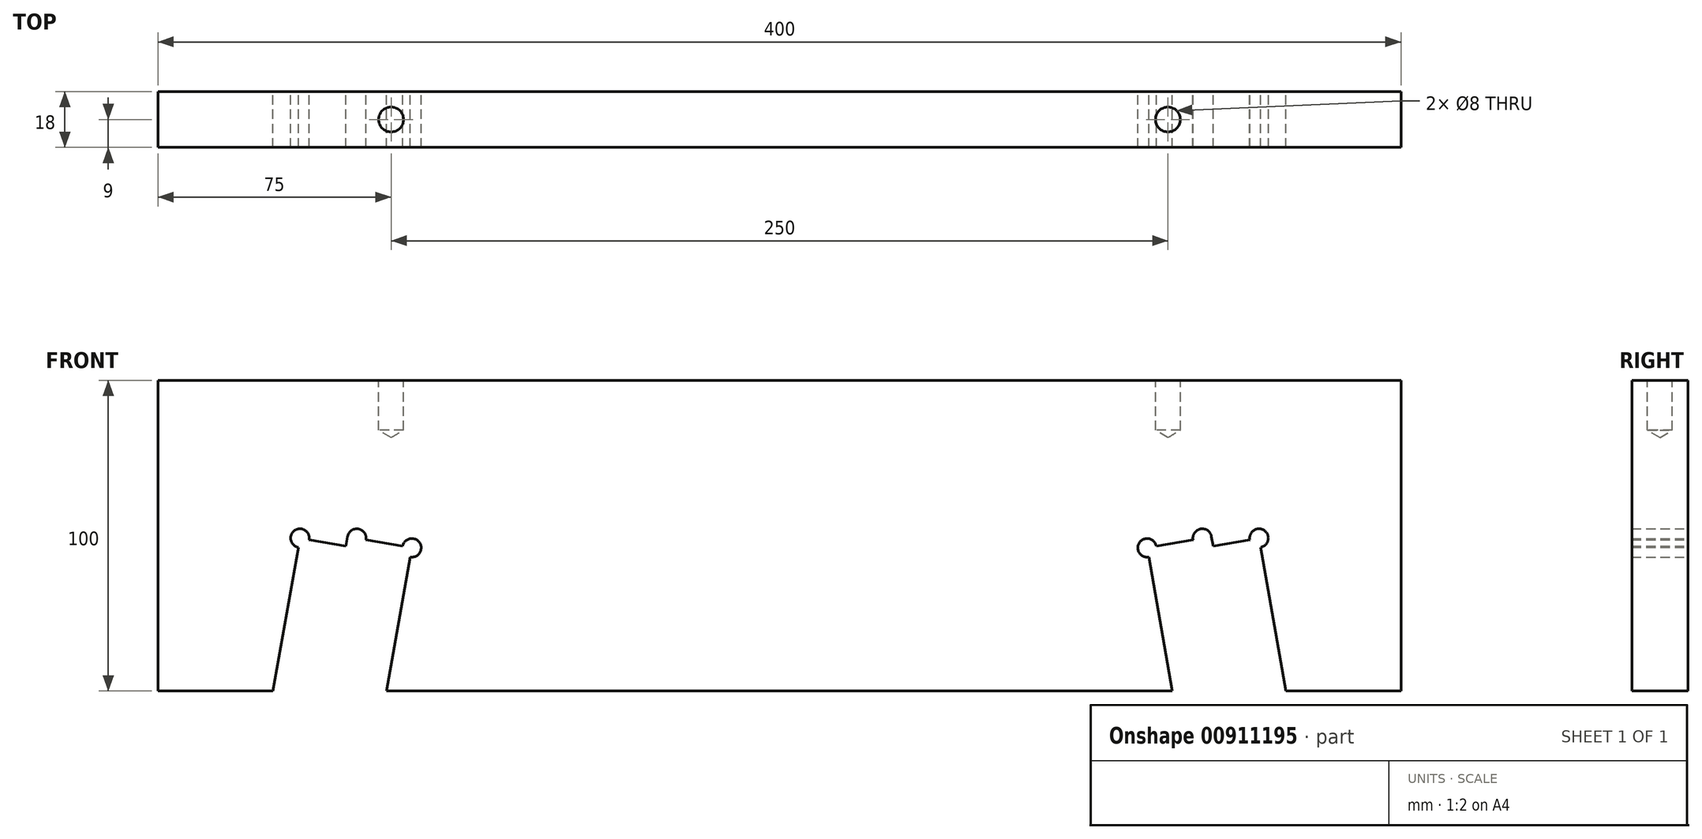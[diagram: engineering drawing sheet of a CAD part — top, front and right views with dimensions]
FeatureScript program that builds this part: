
annotation { "Feature Type Name" : "Feature", "Feature Type Description" : "" }
export const myFeature = defineFeature(function(context is Context, id is Id, definition is map)
    precondition{}
    {
        {
            var Q0;
            Q0=qCreatedBy(makeId("Front.planeOp"),FACE);
            var sketch = newSketch(context, id + "F0", { "sketchPlane" : qUnion([Q0])});
            skLineSegment(sketch, "E0", {"start": v(0, 0) * mm, "end": v(400, 0) * mm});
            skLineSegment(sketch, "E1", {"start": v(400, 0) * mm, "end": v(400, -100) * mm});
            skLineSegment(sketch, "E2", {"start": v(0, -100) * mm, "end": v(0, 0) * mm});
            skLineSegment(sketch, "E3", {"start": v(0, -100) * mm, "end": v(37, -100) * mm});
            skLineSegment(sketch, "E4", {"start": v(37, -100) * mm, "end": v(45.68, -50.76) * mm});
            skLineSegment(sketch, "E5", {"start": v(363, -100) * mm, "end": v(354.32, -50.76) * mm});
            skLineSegment(sketch, "E6", {"start": v(354.32, -50.76) * mm, "end": v(339.55, -53.36) * mm});
            skLineSegment(sketch, "E7", {"start": v(333.09, -51.28) * mm, "end": v(318.31, -53.89) * mm});
            skLineSegment(sketch, "E8", {"start": v(326.44, -100) * mm, "end": v(318.31, -53.89) * mm});
            skLineSegment(sketch, "E9", {"start": v(45.68, -50.76) * mm, "end": v(60.45, -53.36) * mm});
            skLineSegment(sketch, "E10", {"start": v(66.91, -51.28) * mm, "end": v(81.69, -53.89) * mm});
            skLineSegment(sketch, "E11", {"start": v(81.69, -53.89) * mm, "end": v(73.56, -100) * mm});
            skLineSegment(sketch, "E12", {"start": v(73.56, -100) * mm, "end": v(326.44, -100) * mm});
            skLineSegment(sketch, "E13", {"start": v(363, -100) * mm, "end": v(400, -100) * mm});
            skLineSegment(sketch, "E14", {"start": v(45.68, -50.76) * mm, "end": v(45.16, -53.71) * mm});
            skLineSegment(sketch, "E15", {"start": v(45.68, -50.76) * mm, "end": v(48.64, -51.28) * mm});
            skArc(sketch, "E16", {"start": v(48.64, -51.28) * mm, "mid": v(43.96, -48.3) * mm, "end": v(45.16, -53.71) * mm});
            skArc(sketch, "E17", {"start": v(66.91, -51.28) * mm, "mid": v(64.48, -47.8) * mm, "end": v(61, -50.24) * mm});
            skLineSegment(sketch, "E18", {"start": v(61, -50.24) * mm, "end": v(60.45, -53.36) * mm});
            skLineSegment(sketch, "E19", {"start": v(81.69, -53.89) * mm, "end": v(78.73, -53.36) * mm});
            skLineSegment(sketch, "E20", {"start": v(81.69, -53.89) * mm, "end": v(81.17, -56.84) * mm});
            skArc(sketch, "E21", {"start": v(81.17, -56.84) * mm, "mid": v(84.14, -52.16) * mm, "end": v(78.73, -53.36) * mm});
            skArc(sketch, "E22", {"start": v(339, -50.24) * mm, "mid": v(335.52, -47.8) * mm, "end": v(333.09, -51.28) * mm});
            skLineSegment(sketch, "E23", {"start": v(339, -50.24) * mm, "end": v(339.55, -53.36) * mm});
            skLineSegment(sketch, "E24", {"start": v(318.31, -53.89) * mm, "end": v(318.83, -56.84) * mm});
            skLineSegment(sketch, "E25", {"start": v(318.31, -53.89) * mm, "end": v(321.27, -53.36) * mm});
            skLineSegment(sketch, "E26", {"start": v(354.32, -50.76) * mm, "end": v(351.36, -51.28) * mm});
            skLineSegment(sketch, "E27", {"start": v(354.32, -50.76) * mm, "end": v(354.84, -53.71) * mm});
            skArc(sketch, "E28", {"start": v(321.27, -53.36) * mm, "mid": v(315.86, -52.16) * mm, "end": v(318.83, -56.84) * mm});
            skArc(sketch, "E29", {"start": v(354.84, -53.71) * mm, "mid": v(356.04, -48.3) * mm, "end": v(351.36, -51.28) * mm});
            skSolve(sketch);
        }
        {
            var Q0;
            Q0=makeQuery(id+"F0.imprint","IMPRINT",FACE,{"disambiguationData":[TD([[makeQuery(id+"F0.imprint","IMPRINT",EDGE,{"derivedFrom":sQuery(id+"F0.wireOp",EDGE,"E0")}),-1.0]])]});
            extrude(context, id + "F1", {"entities" : qUnion([Q0]), "depth" : 18 * mm, "offsetDistance" : 25 * mm});
        }
        {
            var Q0;
            Q0=makeQuery(id+"F1.opExtrude","SWEPT_FACE",FACE,{"disambiguationData":[OSD([sQuery(id+"F0.wireOp",EDGE,"E0")])]});
            var sketch = newSketch(context, id + "F2", { "sketchPlane" : qUnion([Q0])});
            skCircle(sketch, "E30", {"center": v(600, -9) * mm, "radius": 4 * mm});
            skLineSegment(sketch, "E31", {"start": v(0, -9) * mm, "end": v(75, -9) * mm});
            skLineSegment(sketch, "E32", {"start": v(400, -9) * mm, "end": v(325, -9) * mm});
            skCircle(sketch, "E33", {"center": v(75, -9) * mm, "radius": 4 * mm});
            skCircle(sketch, "E34", {"center": v(325, -9) * mm, "radius": 4 * mm});
            skSolve(sketch);
        }
        {
            var Q0;
            Q0=sQuery(id+"F2.wireOp",VERTEX,"E31.end");
            var Q1;
            Q1=sQuery(id+"F2.wireOp",VERTEX,"E32.end");
            var Q2;
            Q2=makeQuery(id+"F1.opExtrude","SWEPT_BODY",BODY,{"disambiguationData":[OSD([sQuery(id+"F0.wireOp",EDGE,"E0"),sQuery(id+"F0.wireOp",EDGE,"E1"),sQuery(id+"F0.wireOp",EDGE,"E2"),sQuery(id+"F0.wireOp",EDGE,"E3"),sQuery(id+"F0.wireOp",EDGE,"E4"),sQuery(id+"F0.wireOp",EDGE,"p948Vvx2-BpZs-LjeI-DL7u-JcSPTKm9zR2G"),sQuery(id+"F0.wireOp",EDGE,"E5"),sQuery(id+"F0.wireOp",EDGE,"E6"),sQuery(id+"F0.wireOp",EDGE,"E7"),sQuery(id+"F0.wireOp",EDGE,"E8"),sQuery(id+"F0.wireOp",EDGE,"tJL5BSTQ-vPUy-ZBqp-yD1B-r7N65kKsLTub"),sQuery(id+"F0.wireOp",EDGE,"E9"),sQuery(id+"F0.wireOp",EDGE,"E10"),sQuery(id+"F0.wireOp",EDGE,"E11"),sQuery(id+"F0.wireOp",EDGE,"7mRe4zCy-AX93-jLrA-rvQe-SIDqEoWd2NOy"),sQuery(id+"F0.wireOp",EDGE,"E12")])]});
            hole(context, id + "F3", {"style" : HoleStyle.SIMPLE, "endStyle" : HoleEndStyle.BLIND, "holeDiameter" : 8 * mm, "majorDiameter" : 5 * mm, "holeDepth" : 16 * mm, "isTappedThrough" : true, "tappedDepth" : 12 * mm, "tapClearance" : 3, "locations" : qUnion([Q0, Q1]), "scope" : qUnion([Q2])});
        }
    });
